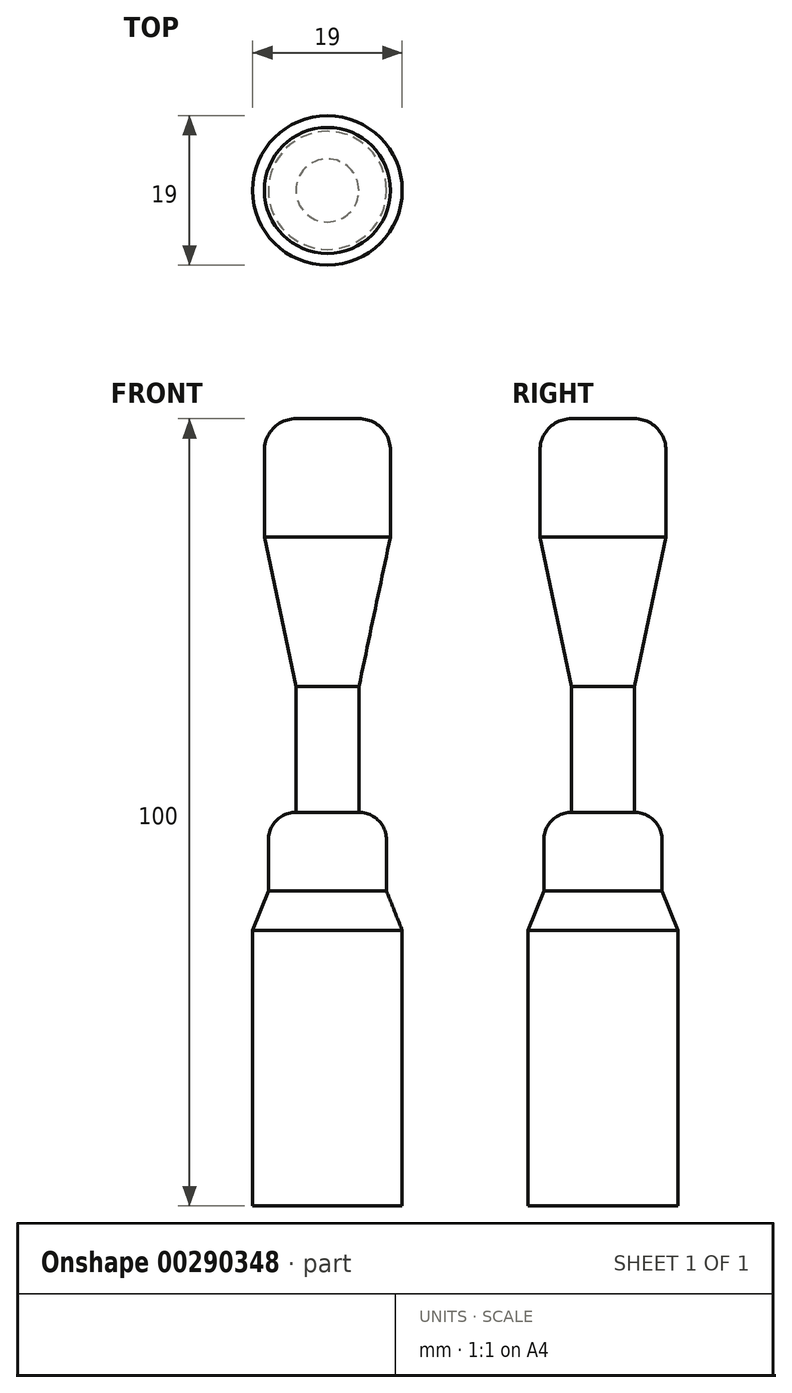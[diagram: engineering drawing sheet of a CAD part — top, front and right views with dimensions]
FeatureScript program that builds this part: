
annotation { "Feature Type Name" : "Feature", "Feature Type Description" : "" }
export const myFeature = defineFeature(function(context is Context, id is Id, definition is map)
    precondition{}
    {
        {
            var Q0;
            Q0=qCreatedBy(makeId("Front.planeOp"),FACE);
            var sketch = newSketch(context, id + "F0", { "sketchPlane" : qUnion([Q0])});
            skLineSegment(sketch, "E0", {"start": v(0, 0) * mm, "end": v(4, 0) * mm});
            skArc(sketch, "E1", {"start": v(8, -4) * mm, "mid": v(6.83, -1.17) * mm, "end": v(4, 0) * mm});
            skLineSegment(sketch, "E2", {"start": v(8, -4) * mm, "end": v(8, -15) * mm});
            skLineSegment(sketch, "E3", {"start": v(8, -15) * mm, "end": v(4, -34) * mm});
            skLineSegment(sketch, "E4", {"start": v(4, -34) * mm, "end": v(4, -50) * mm});
            skLineSegment(sketch, "E5", {"start": v(7.5, -60) * mm, "end": v(9.5, -65) * mm});
            skLineSegment(sketch, "E6", {"start": v(9.5, -65) * mm, "end": v(9.5, -100) * mm});
            skLineSegment(sketch, "E7", {"start": v(9.5, -100) * mm, "end": v(0, -100) * mm});
            skLineSegment(sketch, "E8", {"start": v(0, -100) * mm, "end": v(0, 0) * mm});
            skLineSegment(sketch, "E9", {"start": v(7.5, -60) * mm, "end": v(7.5, -53.5) * mm});
            skArc(sketch, "E10", {"start": v(7.5, -53.5) * mm, "mid": v(6.47, -51.03) * mm, "end": v(4, -50) * mm});
            skSolve(sketch);
        }
        {
            var Q0;
            Q0=sQuery(id+"F0.wireOp",EDGE,"E7");
            var Q1;
            Q1=sQuery(id+"F0.wireOp",EDGE,"E6");
            var Q2;
            Q2=sQuery(id+"F0.wireOp",EDGE,"E5");
            var Q3;
            Q3=sQuery(id+"F0.wireOp",EDGE,"E9");
            var Q4;
            Q4=sQuery(id+"F0.wireOp",EDGE,"E10");
            var Q5;
            Q5=sQuery(id+"F0.wireOp",EDGE,"E4");
            var Q6;
            Q6=sQuery(id+"F0.wireOp",EDGE,"E3");
            var Q7;
            Q7=sQuery(id+"F0.wireOp",EDGE,"E2");
            var Q8;
            Q8=sQuery(id+"F0.wireOp",EDGE,"E1");
            var Q9;
            Q9=sQuery(id+"F0.wireOp",EDGE,"E0");
            var Q10;
            Q10=sQuery(id+"F0.wireOp",EDGE,"E8");
            revolve(context, id + "F1", {"bodyType" : ToolBodyType.SURFACE, "surfaceEntities" : qUnion([Q0, Q1, Q2, Q3, Q4, Q5, Q6, Q7, Q8, Q9]), "axis" : qUnion([Q10]), "revolveType" : RevolveType.FULL});
        }
    });
